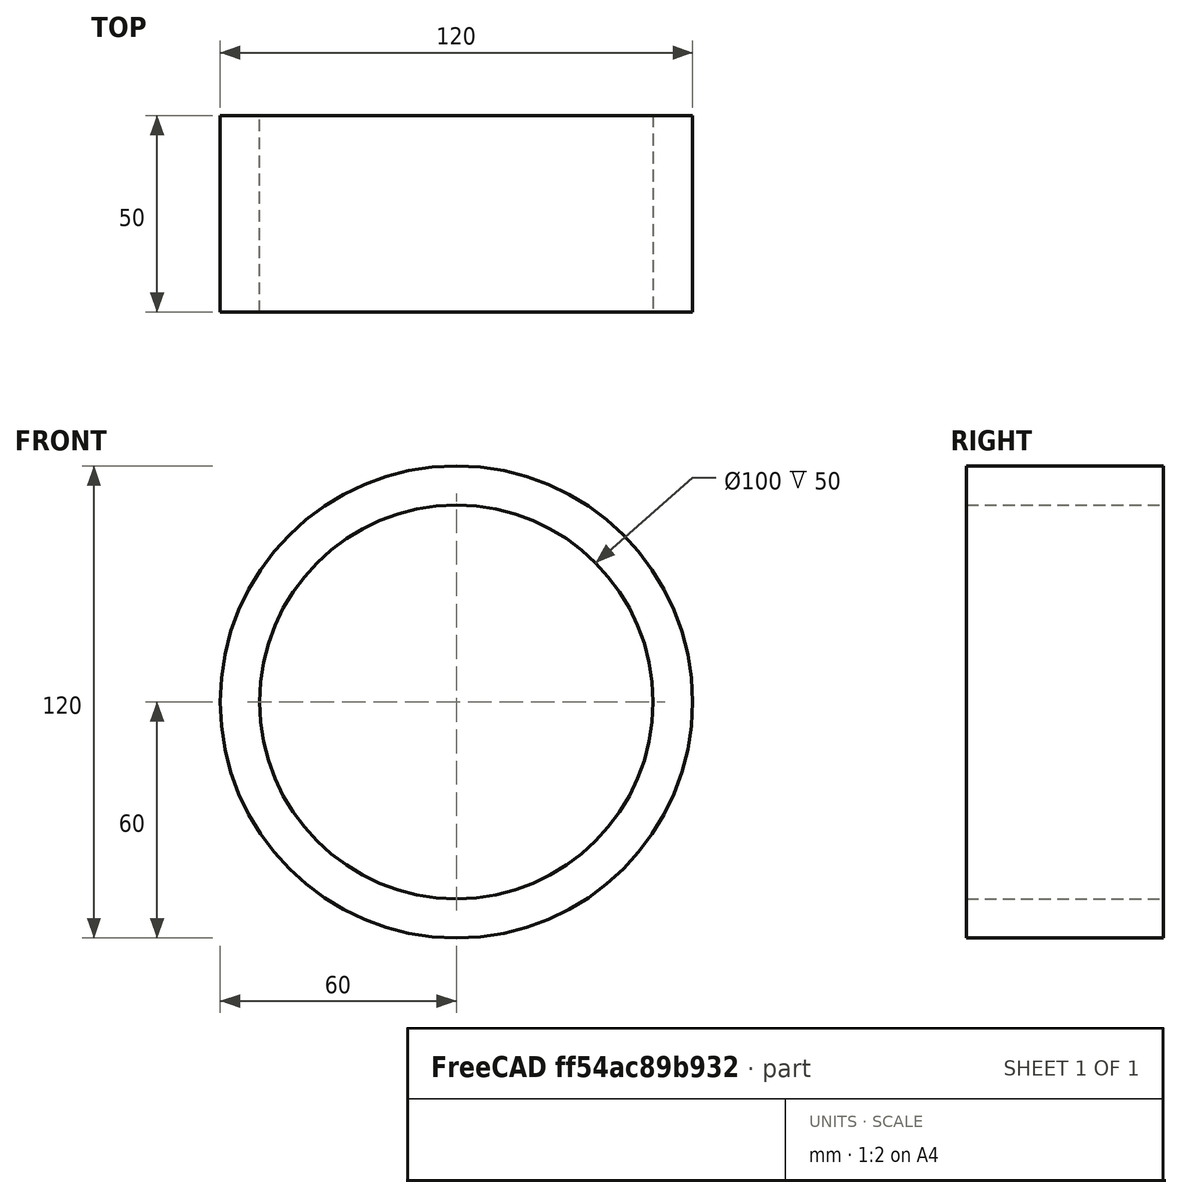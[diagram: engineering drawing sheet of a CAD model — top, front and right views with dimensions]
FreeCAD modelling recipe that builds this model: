
FCSTD DOCUMENT  (FreeCAD 0.14R3700 (Git))
Label: protege sonette
License: CC-BY 3.0
LicenseURL: http://creativecommons.org/licenses/by/3.0/
objects: Sketcher::SketchObject×1, PartDesign::Pad×1
note: 3 computed .brp shape members not serialized (recipe doc carries the construction recipe); baked Part::Feature solids carry a one-line shape summary decoded from their .brp

FEATURE [Sketcher::SketchObject] Sketch
  Placement = pos=(0,0,0) rot=(-1,0,0;4.71239rad)
  sketch-geometry (3):
    g0: Circle CenterX=0 CenterY=0 CenterZ=0 NormalX=0 NormalY=0 NormalZ=1 Radius=50
    g1: Circle CenterX=0 CenterY=0 CenterZ=0 NormalX=0 NormalY=0 NormalZ=1 Radius=60
    g2: LineSegment StartX=-70 StartY=0 StartZ=0 EndX=82.8902 EndY=0 EndZ=0
  constraints (5):
    c: Radius(g0) = 50
    c: Coincident(g1,g-1)
    c: Radius(g1) = 60
    c: PointOnObject(g2,g-1)
    c: Horizontal(g2)
FEATURE [PartDesign::Pad] Pad
  Length = 50
  Length2 = 100
  Placement = pos=(0,0,0) rot=(-1,0,0;4.71239rad)
  Sketch = -> Sketch
  Type = 0
